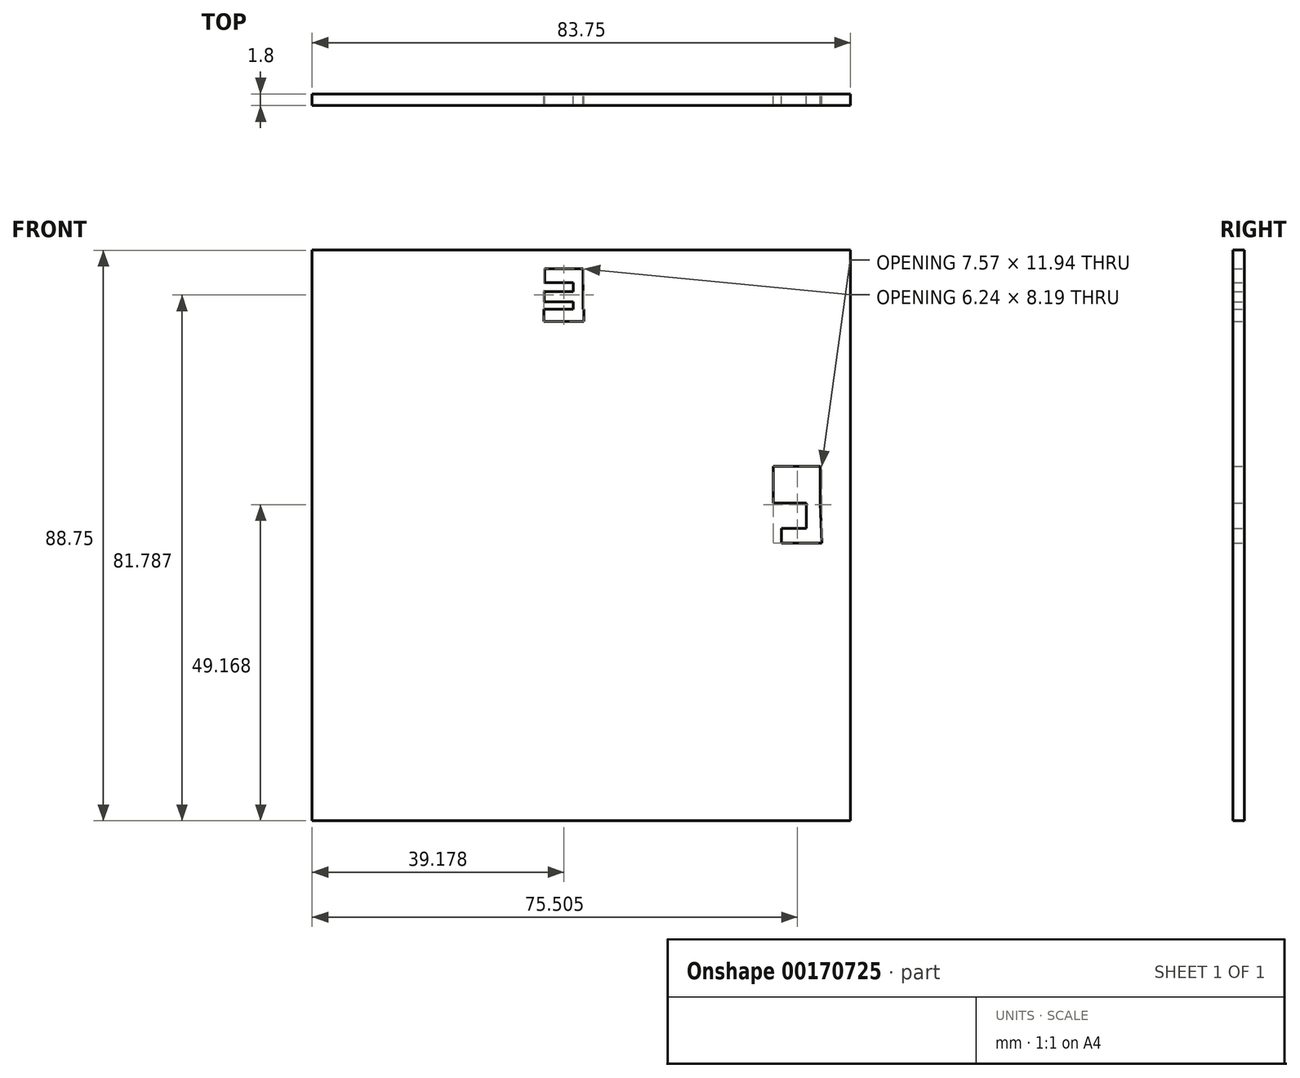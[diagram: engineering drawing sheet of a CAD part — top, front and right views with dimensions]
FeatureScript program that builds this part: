
annotation { "Feature Type Name" : "Feature", "Feature Type Description" : "" }
export const myFeature = defineFeature(function(context is Context, id is Id, definition is map)
    precondition{}
    {
        {
            var Q0;
            Q0=qCreatedBy(makeId("Front.planeOp"),FACE);
            var sketch = newSketch(context, id + "F0", { "sketchPlane" : qUnion([Q0])});
            skLineSegment(sketch, "E0.bottom", {"start": v(-17.7, 67.95) * mm, "end": v(66.04, 67.95) * mm});
            skLineSegment(sketch, "E0.top", {"start": v(-17.7, -20.8) * mm, "end": v(66.04, -20.8) * mm});
            skLineSegment(sketch, "E0.left", {"start": v(-17.7, 67.95) * mm, "end": v(-17.7, -20.8) * mm});
            skLineSegment(sketch, "E0.right", {"start": v(66.04, 67.95) * mm, "end": v(66.04, -20.8) * mm});
            skLineSegment(sketch, "E1.bottom", {"start": v(18.48, 65.08) * mm, "end": v(24.42, 65.08) * mm});
            skLineSegment(sketch, "E1.top", {"start": v(18.48, 62.89) * mm, "end": v(22.94, 62.89) * mm});
            skLineSegment(sketch, "E1.left", {"start": v(18.48, 65.08) * mm, "end": v(18.48, 62.89) * mm});
            skLineSegment(sketch, "E1.right", {"start": v(24.42, 65.08) * mm, "end": v(24.42, 62.89) * mm});
            skLineSegment(sketch, "E2.bottom", {"start": v(18.4, 61.49) * mm, "end": v(22.94, 61.49) * mm});
            skLineSegment(sketch, "E2.top", {"start": v(18.4, 59.9) * mm, "end": v(22.94, 59.9) * mm});
            skLineSegment(sketch, "E2.left", {"start": v(18.4, 61.49) * mm, "end": v(18.4, 59.9) * mm});
            skLineSegment(sketch, "E2.right", {"start": v(24.35, 61.49) * mm, "end": v(24.35, 59.9) * mm});
            skLineSegment(sketch, "E3.bottom", {"start": v(18.35, 58.8) * mm, "end": v(22.94, 58.8) * mm});
            skLineSegment(sketch, "E3.top", {"start": v(18.35, 56.9) * mm, "end": v(24.59, 56.9) * mm});
            skLineSegment(sketch, "E3.left", {"start": v(18.35, 58.8) * mm, "end": v(18.35, 56.9) * mm});
            skLineSegment(sketch, "E3.right", {"start": v(24.59, 58.8) * mm, "end": v(24.59, 56.9) * mm});
            skLineSegment(sketch, "E4.bottom", {"start": v(24.42, 65.08) * mm, "end": v(22.94, 65.08) * mm});
            skLineSegment(sketch, "E4.top", {"start": v(24.42, 56.9) * mm, "end": v(22.94, 56.9) * mm});
            skLineSegment(sketch, "E4.left", {"start": v(24.42, 65.08) * mm, "end": v(24.42, 56.9) * mm});
            skLineSegment(sketch, "E4.right", {"start": v(22.94, 62.89) * mm, "end": v(22.94, 61.49) * mm});
            skLineSegment(sketch, "E5.trimOffspring", {"start": v(22.94, 59.9) * mm, "end": v(22.94, 58.8) * mm});
            skLineSegment(sketch, "E6.trimOffspring", {"start": v(24.42, 58.8) * mm, "end": v(24.59, 58.8) * mm});
            skLineSegment(sketch, "E7", {"start": v(54.01, 34.34) * mm, "end": v(61.34, 34.34) * mm});
            skLineSegment(sketch, "E8", {"start": v(61.33, 34.65) * mm, "end": v(61.34, 28.6) * mm});
            skLineSegment(sketch, "E9", {"start": v(59.2, 28.6) * mm, "end": v(54.01, 28.6) * mm});
            skLineSegment(sketch, "E10", {"start": v(54.01, 34.34) * mm, "end": v(54.01, 28.6) * mm});
            skLineSegment(sketch, "E11", {"start": v(56.08, 32.84) * mm, "end": v(56.08, 30.59) * mm});
            skLineSegment(sketch, "E12", {"start": v(56.08, 30.59) * mm, "end": v(59.2, 30.59) * mm});
            skLineSegment(sketch, "E13", {"start": v(59.2, 30.59) * mm, "end": v(59.2, 32.84) * mm});
            skLineSegment(sketch, "E14", {"start": v(59.2, 32.84) * mm, "end": v(56.08, 32.84) * mm});
            skLineSegment(sketch, "E15", {"start": v(59.2, 28.6) * mm, "end": v(59.2, 24.65) * mm});
            skLineSegment(sketch, "E16", {"start": v(59.2, 24.65) * mm, "end": v(55.28, 24.65) * mm});
            skLineSegment(sketch, "E17", {"start": v(55.28, 24.65) * mm, "end": v(55.28, 22.4) * mm});
            skLineSegment(sketch, "E18", {"start": v(55.27, 22.4) * mm, "end": v(61.6, 22.4) * mm});
            skLineSegment(sketch, "E19", {"start": v(61.58, 22.4) * mm, "end": v(61.34, 28.6) * mm});
            skPoint(sketch, "E20.orphan", {"position": v(59.2, 30.26) * mm});
            skSolve(sketch);
        }
        {
            var Q0;
            Q0 = qSketchRegion(id + "F0", true);
            extrude(context, id + "F1", {"entities" : qUnion([Q0]), "depth" : 1.8 * mm});
        }
    });
